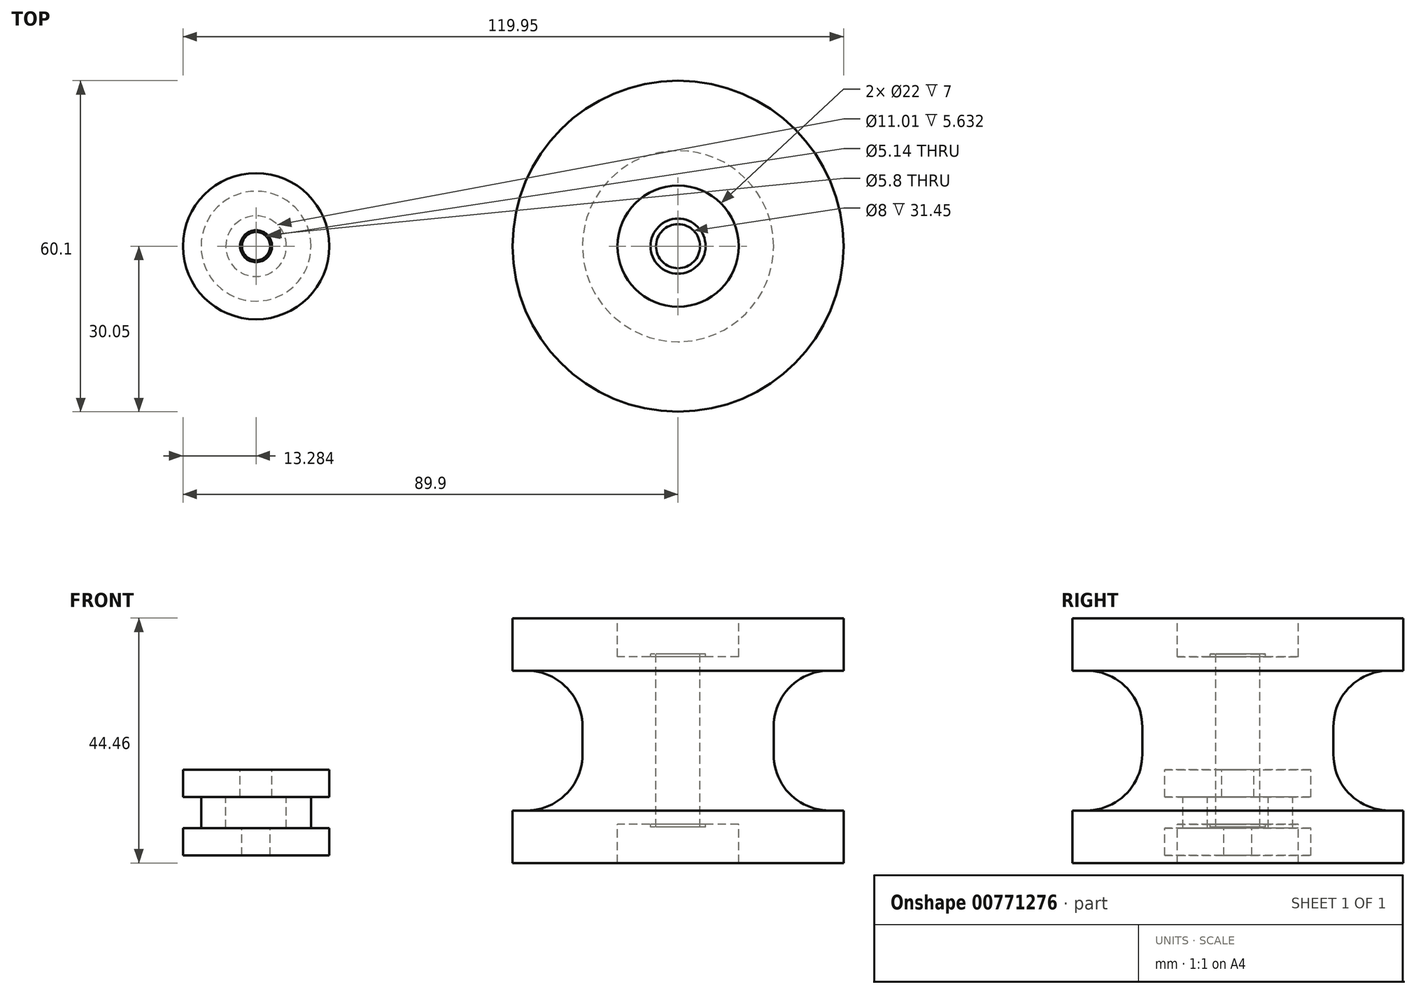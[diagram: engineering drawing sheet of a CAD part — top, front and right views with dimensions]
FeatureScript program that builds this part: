
annotation { "Feature Type Name" : "Feature", "Feature Type Description" : "" }
export const myFeature = defineFeature(function(context is Context, id is Id, definition is map)
    precondition{}
    {
        {
            var Q0;
            Q0=qCreatedBy(makeId("Front.planeOp"),FACE);
            var sketch = newSketch(context, id + "F0", { "sketchPlane" : qUnion([Q0])});
            skLineSegment(sketch, "E0", {"start": v(17.35, 0) * mm, "end": v(17.35, 2.54) * mm});
            skLineSegment(sketch, "E1", {"start": v(17.35, 22.23) * mm, "end": v(11, 22.23) * mm});
            skLineSegment(sketch, "E2", {"start": v(11, 22.22) * mm, "end": v(11, 15.22) * mm});
            skLineSegment(sketch, "E3", {"start": v(11, 15.22) * mm, "end": v(5, 15.22) * mm});
            skLineSegment(sketch, "E4", {"start": v(5, 15.22) * mm, "end": v(5, 15.72) * mm});
            skLineSegment(sketch, "E5", {"start": v(5, 15.72) * mm, "end": v(4, 15.72) * mm});
            skLineSegment(sketch, "E6", {"start": v(4, 15.72) * mm, "end": v(4, 0) * mm});
            skLineSegment(sketch, "E7", {"start": v(4, 0) * mm, "end": v(17.35, 0) * mm});
            skLineSegment(sketch, "E8", {"start": v(0, 32.84) * mm, "end": v(0, -12.31) * mm, "construction": true});
            skLineSegment(sketch, "E9.MirrorCS", {"start": v(5, -15.22) * mm, "end": v(5, -15.72) * mm});
            skLineSegment(sketch, "E10.MirrorCS", {"start": v(11, -15.22) * mm, "end": v(5, -15.22) * mm});
            skLineSegment(sketch, "E11.MirrorCS", {"start": v(11, -22.22) * mm, "end": v(11, -15.22) * mm});
            skLineSegment(sketch, "E12.MirrorCS", {"start": v(17.35, -22.23) * mm, "end": v(11, -22.23) * mm});
            skLineSegment(sketch, "E13.MirrorCS", {"start": v(17.35, 0) * mm, "end": v(17.35, -2.54) * mm});
            skLineSegment(sketch, "E14.MirrorCS", {"start": v(5, -15.72) * mm, "end": v(4, -15.72) * mm});
            skLineSegment(sketch, "E15.MirrorCS", {"start": v(4, -15.72) * mm, "end": v(4, 0) * mm});
            skLineSegment(sketch, "E16", {"start": v(17.35, 22.22) * mm, "end": v(30.05, 22.22) * mm});
            skLineSegment(sketch, "E17", {"start": v(30.05, 22.23) * mm, "end": v(30.05, 12.7) * mm});
            skLineSegment(sketch, "E18", {"start": v(30.05, 12.7) * mm, "end": v(27.51, 12.7) * mm});
            skLineSegment(sketch, "E19.MirrorCS", {"start": v(17.35, -22.22) * mm, "end": v(30.05, -22.22) * mm});
            skLineSegment(sketch, "E20.MirrorCS", {"start": v(30.05, -22.23) * mm, "end": v(30.05, -12.7) * mm});
            skPoint(sketch, "E21.newPointB", {"position": v(17.35, 22.22) * mm});
            skArc(sketch, "E21.filletArc", {"start": v(27.51, 12.7) * mm, "mid": v(20.33, 9.72) * mm, "end": v(17.35, 2.54) * mm});
            skArc(sketch, "E22.MirrorCS", {"start": v(27.5, -12.7) * mm, "mid": v(20.33, -9.72) * mm, "end": v(17.35, -2.54) * mm});
            skPoint(sketch, "E23.MirrorCS.start.orphan", {"position": v(30.05, -12.7) * mm});
            skPoint(sketch, "E24.MirrorCS.end.orphan", {"position": v(17.35, -22.23) * mm});
            skLineSegment(sketch, "E25.MirrorCS", {"start": v(30.05, -12.7) * mm, "end": v(27.51, -12.7) * mm});
            skSolve(sketch);
        }
        {
            var Q0;
            Q0=makeQuery(id+"F0.imprint","IMPRINT",FACE,{"disambiguationData":[TD([[makeQuery(id+"F0.imprint","IMPRINT",EDGE,{"derivedFrom":sQuery(id+"F0.wireOp",EDGE,"E0")}),1.0]])]});
            var Q1;
            Q1=makeQuery(id+"F0.imprint","IMPRINT",FACE,{"disambiguationData":[TD([[makeQuery(id+"F0.imprint","IMPRINT",EDGE,{"derivedFrom":sQuery(id+"F0.wireOp",EDGE,"E9.MirrorCS")}),-1.0]])]});
            var Q2;
            Q2=sQuery(id+"F0.wireOp",EDGE,"E8");
            revolve(context, id + "F1", {"surfaceOperationType" : NewSurfaceOperationType.NEW, "entities" : qUnion([Q0, Q1]), "axis" : qUnion([Q2]), "revolveType" : RevolveType.FULL});
        }
        {
            var Q0;
            Q0=qCreatedBy(makeId("Front.planeOp"),FACE);
            var sketch = newSketch(context, id + "F2", { "sketchPlane" : qUnion([Q0])});
            skLineSegment(sketch, "E26.left", {"start": v(-71.11, -15.9) * mm, "end": v(-71.11, -10.27) * mm});
            skLineSegment(sketch, "E26.right", {"start": v(-66.63, -15.9) * mm, "end": v(-66.63, -10.27) * mm});
            skLineSegment(sketch, "E27", {"start": v(-71.11, -10.27) * mm, "end": v(-73.72, -10.27) * mm});
            skLineSegment(sketch, "E28", {"start": v(-73.72, -10.27) * mm, "end": v(-73.72, -5.3) * mm});
            skLineSegment(sketch, "E29", {"start": v(-73.72, -5.3) * mm, "end": v(-63.33, -5.3) * mm});
            skLineSegment(sketch, "E30", {"start": v(-63.33, -5.3) * mm, "end": v(-63.33, -10.27) * mm});
            skLineSegment(sketch, "E31", {"start": v(-63.33, -10.27) * mm, "end": v(-66.63, -10.27) * mm});
            skLineSegment(sketch, "E32", {"start": v(-71.11, -15.9) * mm, "end": v(-74.05, -15.9) * mm});
            skLineSegment(sketch, "E33", {"start": v(-74.05, -15.9) * mm, "end": v(-74.05, -20.87) * mm});
            skLineSegment(sketch, "E34", {"start": v(-74.05, -20.87) * mm, "end": v(-63.33, -20.87) * mm});
            skLineSegment(sketch, "E35", {"start": v(-63.33, -20.87) * mm, "end": v(-63.33, -15.9) * mm});
            skLineSegment(sketch, "E36", {"start": v(-63.33, -15.9) * mm, "end": v(-66.63, -15.9) * mm});
            skLineSegment(sketch, "E37", {"start": v(-76.62, 0) * mm, "end": v(-76.62, -31.14) * mm});
            skSolve(sketch);
        }
        {
            var Q0;
            Q0=makeQuery(id+"F2.imprint","IMPRINT",FACE,{"disambiguationData":[TD([[makeQuery(id+"F2.imprint","IMPRINT",EDGE,{"derivedFrom":sQuery(id+"F2.wireOp",EDGE,"E26.left")}),-1.0]])]});
            var Q1;
            Q1=sQuery(id+"F2.wireOp",EDGE,"E37");
            revolve(context, id + "F3", {"surfaceOperationType" : NewSurfaceOperationType.NEW, "entities" : qUnion([Q0]), "axis" : qUnion([Q1]), "revolveType" : RevolveType.FULL});
        }
    });
